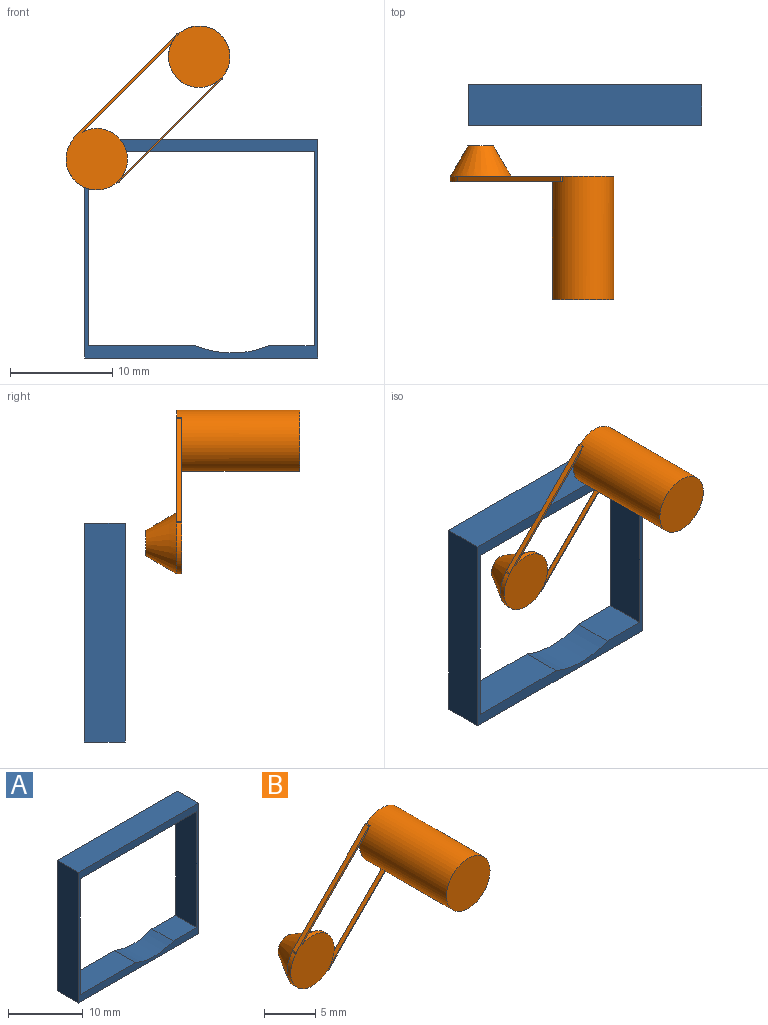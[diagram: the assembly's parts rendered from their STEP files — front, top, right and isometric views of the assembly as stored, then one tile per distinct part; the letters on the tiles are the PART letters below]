
ASSEMBLY  parts=2 mates=1
PART A: 14 faces, bbox 22.8x4x21.4 mm
  f0: cylinder r=3.5mm len=3.5mm, axis (0,1,0), area 16.5mm2, adj f1,f2,f3,f4
  f1: plane 3.5x3.5mm, normal (0,-1,0), area 2.6mm2, adj f0,f3,f4
  f2: plane 22.75x21.38mm, normal (0,1,0), area 67.6mm2, adj f0,f3,f4,f5,f6,f7,f8,f9
  f3: plane 19x4mm, normal (1,0,0), area 65.5mm2, adj f0,f1,f2,f4,f6,f13
  f4: plane 22x4mm, normal (0,0,-1), area 77.5mm2, adj f0,f1,f2,f3,f7,f13
  f5: cylinder r=9.21mm len=7.07mm, axis (0,1,0), area 29mm2, adj f2,f6,f12,f13
  f6: plane 10.46x4mm, normal (0,0,1), area 41.9mm2, adj f2,f3,f5,f13
  f7: plane 19x4mm, normal (-1,0,0), area 76mm2, adj f2,f4,f12,f13
  f8: plane 21.38x4mm, normal (1,0,0), area 85.5mm2, adj f2,f9,f11,f13
  f9: plane 22.75x4mm, normal (0,0,1), area 91mm2, adj f2,f8,f10,f13
  f10: plane 21.38x4mm, normal (-1,0,0), area 85.5mm2, adj f2,f9,f11,f13
  f11: plane 22.75x4mm, normal (0,0,-1), area 91mm2, adj f2,f8,f10,f13
  f12: plane 4.46x4mm, normal (0,0,1), area 17.9mm2, adj f2,f5,f7,f13
  f13: plane 22.75x21.38mm, normal (0,-1,0), area 65mm2, adj f3,f4,f5,f6,f7,f8,f9,f10
PART B: 16 faces, bbox 16x15x16 mm
  f0: plane 2.5x2.5mm, normal (0,1,0), area 4.9mm2, adj f1
  f1: cone r=1.25mm half-angle=30.3deg, axis (0,-1,0), area 46.4mm2, adj f0,f2,f14,f15
  f2: plane 15.3x15.25mm, normal (0,1,0), area 33.5mm2, adj f1,f3,f4,f5,f7,f8,f9,f10
  f3: plane 8.79x8.79mm, normal (0.71,0,-0.71), area 6.2mm2, adj f2,f5,f11,f14
  f4: cylinder r=0.12mm len=0.5mm, axis (0,1,0), area 0.1mm2, adj f2,f11,f13,f15
  f5: cylinder r=3mm len=12mm, axis (0,1,0), area 225.6mm2, adj f2,f3,f6,f7,f8,f11,f12
  f6: plane 6x6mm, normal (0,-1,0), area 28.3mm2, adj f5
  f7: cylinder r=0.12mm len=0.5mm, axis (0,1,0), area 0.1mm2, adj f2,f5,f10,f11
  f8: plane 10x10mm, normal (-0.71,0,0.71), area 7.1mm2, adj f2,f5,f11,f14
  f9: cylinder r=0.12mm len=0.5mm, axis (0,1,0), area 0.1mm2, adj f2,f10,f11,f15
  f10: plane 10x10mm, normal (0.71,0,-0.71), area 7.1mm2, adj f2,f7,f9,f11
  f11: plane 15.25x15.24mm, normal (0,-1,0), area 33.5mm2, adj f3,f4,f5,f7,f8,f9,f10,f12
  f12: cylinder r=0.12mm len=0.5mm, axis (0,1,0), area 0.1mm2, adj f2,f5,f11,f13
  f13: plane 10.06x10.06mm, normal (-0.71,0,0.71), area 7.1mm2, adj f2,f4,f11,f12
  f14: cylinder r=3mm len=5.12mm, axis (0,1,0), area 4.3mm2, adj f1,f3,f8,f11
  f15: cylinder r=3mm len=5.03mm, axis (0,1,0), area 4.5mm2, adj f1,f4,f9,f11
PLACE A t=(-21.19,0.9,-14.54)mm
PLACE B t=(-31.41,-5.1,-5.82)mm
MATE fastened A.f1 <-> B.f1  axis (0,-1,0) through (-31.41,-2.1,-5.82)mm
